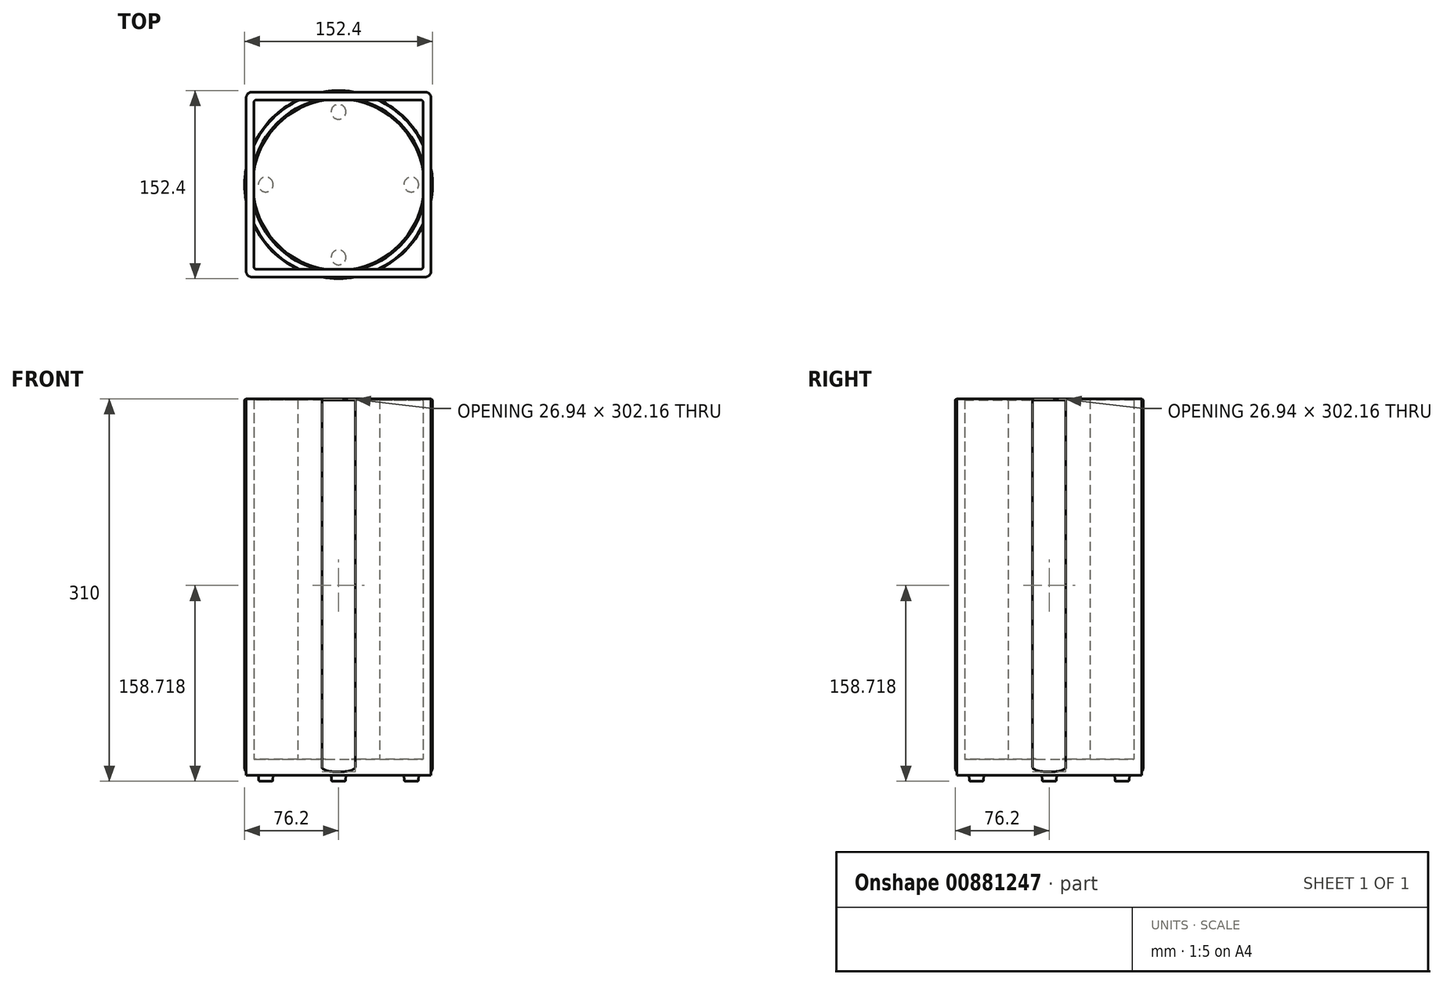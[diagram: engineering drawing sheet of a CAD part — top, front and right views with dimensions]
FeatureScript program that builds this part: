
annotation { "Feature Type Name" : "Feature", "Feature Type Description" : "" }
export const myFeature = defineFeature(function(context is Context, id is Id, definition is map)
    precondition{}
    {
        {
            var Q0;
            Q0=qCreatedBy(makeId("Front.planeOp"),FACE);
            var sketch = newSketch(context, id + "F0", { "sketchPlane" : qUnion([Q0])});
            skLineSegment(sketch, "E0", {"start": v(-43.27, 0) * mm, "end": v(-69.85, 0) * mm});
            skLineSegment(sketch, "E1", {"start": v(-76.2, 6.35) * mm, "end": v(-76.2, 304.8) * mm});
            skLineSegment(sketch, "E2", {"start": v(-76.2, 304.8) * mm, "end": v(-69.85, 304.8) * mm});
            skLineSegment(sketch, "E3", {"start": v(-69.85, 304.8) * mm, "end": v(-69.85, 13.97) * mm});
            skLineSegment(sketch, "E4", {"start": v(-68.58, 12.7) * mm, "end": v(-43.27, 12.7) * mm});
            skLineSegment(sketch, "E5", {"start": v(-42, 11.43) * mm, "end": v(-42, 1.27) * mm});
            skPoint(sketch, "E6.visualSharp", {"position": v(-42, 12.7) * mm});
            skArc(sketch, "E6.filletArc", {"start": v(-42, 11.43) * mm, "mid": v(-42.37, 12.33) * mm, "end": v(-43.27, 12.7) * mm});
            skPoint(sketch, "E7.visualSharp", {"position": v(-42, 0) * mm});
            skArc(sketch, "E7.filletArc", {"start": v(-43.27, 0) * mm, "mid": v(-42.37, 0.37) * mm, "end": v(-42, 1.27) * mm});
            skPoint(sketch, "E8.visualSharp", {"position": v(-76.2, 0) * mm});
            skArc(sketch, "E8.filletArc", {"start": v(-76.2, 6.35) * mm, "mid": v(-74.34, 1.86) * mm, "end": v(-69.85, 0) * mm});
            skPoint(sketch, "E9.visualSharp", {"position": v(-69.85, 12.7) * mm});
            skArc(sketch, "E9.filletArc", {"start": v(-69.85, 13.97) * mm, "mid": v(-69.48, 13.07) * mm, "end": v(-68.58, 12.7) * mm});
            skSolve(sketch);
        }
        {
            var Q0;
            Q0=qCreatedBy(makeId("Front.planeOp"),FACE);
            var sketch = newSketch(context, id + "F1", { "sketchPlane" : qUnion([Q0])});
            skLineSegment(sketch, "E10", {"start": v(0, 0) * mm, "end": v(0, 88.55) * mm, "construction": true});
            skSolve(sketch);
        }
        {
            var Q0;
            Q0=qSketchRegion(id+"F0",true);
            var Q1;
            Q1=sQuery(id+"F1.wireOp",EDGE,"E10");
            revolve(context, id + "F2", {"surfaceOperationType" : NewSurfaceOperationType.NEW, "entities" : qUnion([Q0]), "axis" : qUnion([Q1]), "revolveType" : RevolveType.FULL});
        }
        {
            var Q0;
            Q0=makeQuery(id+"F2.opRevolve","SWEPT_EDGE",EDGE,{"disambiguationData":[OSD([sQuery(id+"F0.wireOp",EDGE,"E2"),sQuery(id+"F0.wireOp",EDGE,"E3")])]});
            var Q1;
            Q1=makeQuery(id+"F2.opRevolve","SWEPT_EDGE",EDGE,{"disambiguationData":[OSD([sQuery(id+"F0.wireOp",EDGE,"E1"),sQuery(id+"F0.wireOp",EDGE,"E2")])]});
            chamfer(context, id + "F3", {"entities" : qUnion([Q0, Q1]), "width" : 0.64 * mm, "tangentPropagation" : true});
        }
        {
            var Q0;
            Q0=makeQuery(id+"F2.opRevolve","SWEPT_FACE",FACE,{"disambiguationData":[OSD([sQuery(id+"F0.wireOp",EDGE,"E0")])]});
            var sketch = newSketch(context, id + "F4", { "sketchPlane" : qUnion([Q0])});
            skCircle(sketch, "E11", {"center": v(0, 59) * mm, "radius": 6 * mm});
            skCircle(sketch, "E12.1.0", {"center": v(-59, 0) * mm, "radius": 6 * mm});
            skCircle(sketch, "E12.2.0", {"center": v(0, -59) * mm, "radius": 6 * mm});
            skCircle(sketch, "E12.3.0", {"center": v(59, 0) * mm, "radius": 6 * mm});
            skPoint(sketch, "E12.center", {"position": v(0, 0) * mm});
            skSolve(sketch);
        }
        {
            var Q0;
            Q0=qSketchRegion(id+"F4",true);
            extrude(context, id + "F5", {"entities" : qUnion([Q0]), "operationType" : NewBodyOperationType.ADD, "depth" : 5 * mm, "offsetDistance" : 25 * mm, "hasDraft" : true, "draftAngle" : 4 * degree, "draftPullDirection" : true});
        }
        {
            var Q0;
            Q0=makeQuery(id+"F5.opExtrude","CAP_FACE",FACE,{"disambiguationData":[OSD([sQuery(id+"F4.wireOp",EDGE,"E11")])],"isStart":false});
            var Q1;
            Q1=makeQuery(id+"F5.opExtrude","CAP_FACE",FACE,{"disambiguationData":[OSD([sQuery(id+"F4.wireOp",EDGE,"E12.1.0")])],"isStart":false});
            var Q2;
            Q2=makeQuery(id+"F5.opExtrude","CAP_FACE",FACE,{"disambiguationData":[OSD([sQuery(id+"F4.wireOp",EDGE,"E12.2.0")])],"isStart":false});
            var Q3;
            Q3=makeQuery(id+"F5.opExtrude","CAP_FACE",FACE,{"disambiguationData":[OSD([sQuery(id+"F4.wireOp",EDGE,"E12.3.0")])],"isStart":false});
            fillet(context, id + "F6", {"entities" : qUnion([Q0, Q1, Q2, Q3]), "radius" : 1 * mm, "tangentPropagation" : true, "allowEdgeOverflow" : false});
        }
        {
            var Q0;
            Q0=qCreatedBy(makeId("Top.planeOp"),FACE);
            var sketch = newSketch(context, id + "F7", { "sketchPlane" : qUnion([Q0])});
            skLineSegment(sketch, "E13.bottom", {"start": v(70, -75) * mm, "end": v(-70, -75) * mm});
            skLineSegment(sketch, "E13.top", {"start": v(70, 75) * mm, "end": v(-70, 75) * mm});
            skLineSegment(sketch, "E13.left", {"start": v(75, -70) * mm, "end": v(75, 70) * mm});
            skLineSegment(sketch, "E13.right", {"start": v(-75, -70) * mm, "end": v(-75, 70) * mm});
            skPoint(sketch, "E13.middle", {"position": v(0, 0) * mm});
            skPoint(sketch, "E14.visualSharp", {"position": v(-75, 75) * mm});
            skArc(sketch, "E14.filletArc", {"start": v(-70, 75) * mm, "mid": v(-73.54, 73.54) * mm, "end": v(-75, 70) * mm});
            skPoint(sketch, "E15.visualSharp", {"position": v(75, 75) * mm});
            skArc(sketch, "E15.filletArc", {"start": v(75, 70) * mm, "mid": v(73.54, 73.54) * mm, "end": v(70, 75) * mm});
            skPoint(sketch, "E16.visualSharp", {"position": v(75, -75) * mm});
            skArc(sketch, "E16.filletArc", {"start": v(70, -75) * mm, "mid": v(73.54, -73.54) * mm, "end": v(75, -70) * mm});
            skPoint(sketch, "E17.visualSharp", {"position": v(-75, -75) * mm});
            skArc(sketch, "E17.filletArc", {"start": v(-75, -70) * mm, "mid": v(-73.54, -73.54) * mm, "end": v(-70, -75) * mm});
            skLineSegment(sketch, "E18.0", {"start": v(68.6, -66.6) * mm, "end": v(68.6, 66.6) * mm});
            skLineSegment(sketch, "E18.1", {"start": v(66.6, -68.6) * mm, "end": v(-66.6, -68.6) * mm});
            skLineSegment(sketch, "E18.2", {"start": v(-68.6, -66.6) * mm, "end": v(-68.6, 66.6) * mm});
            skLineSegment(sketch, "E18.3", {"start": v(66.6, 68.6) * mm, "end": v(-66.6, 68.6) * mm});
            skPoint(sketch, "E19.visualSharp", {"position": v(-68.6, 68.6) * mm});
            skArc(sketch, "E19.filletArc", {"start": v(-66.6, 68.6) * mm, "mid": v(-68.01, 68.01) * mm, "end": v(-68.6, 66.6) * mm});
            skPoint(sketch, "E20.visualSharp", {"position": v(68.6, 68.6) * mm});
            skArc(sketch, "E20.filletArc", {"start": v(68.6, 66.6) * mm, "mid": v(68.01, 68.01) * mm, "end": v(66.6, 68.6) * mm});
            skPoint(sketch, "E21.visualSharp", {"position": v(68.6, -68.6) * mm});
            skArc(sketch, "E21.filletArc", {"start": v(66.6, -68.6) * mm, "mid": v(68.01, -68.01) * mm, "end": v(68.6, -66.6) * mm});
            skPoint(sketch, "E22.visualSharp", {"position": v(-68.6, -68.6) * mm});
            skArc(sketch, "E22.filletArc", {"start": v(-68.6, -66.6) * mm, "mid": v(-68.01, -68.01) * mm, "end": v(-66.6, -68.6) * mm});
            skSolve(sketch);
        }
        {
            var Q0;
            Q0 = qSketchRegion(id + "F7", true);
            extrude(context, id + "F8", {"entities" : qUnion([Q0]), "depth" : 305 * mm, "offsetDistance" : 25 * mm});
        }
        {
            var Q0;
            Q0=makeQuery(id+"F8.opExtrude","CAP_FACE",FACE,{"disambiguationData":[OSD([sQuery(id+"F7.wireOp",EDGE,"E13.bottom"),sQuery(id+"F7.wireOp",EDGE,"E13.top"),sQuery(id+"F7.wireOp",EDGE,"E13.left"),sQuery(id+"F7.wireOp",EDGE,"E13.right"),sQuery(id+"F7.wireOp",EDGE,"E14.filletArc"),sQuery(id+"F7.wireOp",EDGE,"E15.filletArc"),sQuery(id+"F7.wireOp",EDGE,"E16.filletArc"),sQuery(id+"F7.wireOp",EDGE,"E17.filletArc"),sQuery(id+"F7.wireOp",EDGE,"E18.0"),sQuery(id+"F7.wireOp",EDGE,"E18.1"),sQuery(id+"F7.wireOp",EDGE,"E18.2"),sQuery(id+"F7.wireOp",EDGE,"E18.3"),sQuery(id+"F7.wireOp",EDGE,"E19.filletArc"),sQuery(id+"F7.wireOp",EDGE,"E20.filletArc"),sQuery(id+"F7.wireOp",EDGE,"E21.filletArc"),sQuery(id+"F7.wireOp",EDGE,"E22.filletArc")])],"isStart":true});
            var sketch = newSketch(context, id + "F9", { "sketchPlane" : qUnion([Q0])});
            skLineSegment(sketch, "E23.bottom", {"start": v(-68.6, 68.6) * mm, "end": v(68.6, 68.6) * mm});
            skLineSegment(sketch, "E23.top", {"start": v(-68.6, -68.6) * mm, "end": v(68.6, -68.6) * mm});
            skLineSegment(sketch, "E23.left", {"start": v(-68.6, 68.6) * mm, "end": v(-68.6, -68.6) * mm});
            skLineSegment(sketch, "E23.right", {"start": v(68.6, 68.6) * mm, "end": v(68.6, -68.6) * mm});
            skPoint(sketch, "E23.middle", {"position": v(0, 0) * mm});
            skSolve(sketch);
        }
        {
            var Q0;
            Q0 = qSketchRegion(id + "F9", true);
            extrude(context, id + "F10", {"entities" : qUnion([Q0]), "operationType" : NewBodyOperationType.ADD, "oppositeDirection" : true, "depth" : 13 * mm, "offsetDistance" : 25 * mm});
        }
    });
